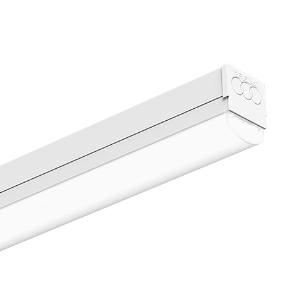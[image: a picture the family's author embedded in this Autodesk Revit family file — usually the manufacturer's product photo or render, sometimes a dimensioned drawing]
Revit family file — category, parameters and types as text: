
# Revit family: 3f_filippi_-_3f_zeta_d_3f_filippi_-_10875_-_3f_zeta_d_2x9_led_l605
name_source: partatom
category: Lighting Fixtures
units: mm (PartAtom-declared; Revit-internal decimal feet)

## family parameters
Cut with Voids When Loaded = No
Host = Face
Light Source = No
Part Type = Normal
Room Calculation Point = No
Round Connector Dimension = Use Diameter
Shared = No

## types (1)
- 3F Filippi - 3F Zeta D (1 x LED, 2418 lm, 20 W, 4000 K)
    Apparent Load = 20 VA
    Approval mark = CE
    CIE Flux Codes = 42 71 90 91 100
    Color Rendering = 80
    Color Temperature = 4000 K
    Control Gear = Electronic ballast
    Default Elevation = 1800 mm
    Description = ILLUMINOTECHNICAL
Luminous efficiency 100% (DLOR 91%, ULOR 9%).
Initial luminous flux of the luminaire 2418 lm.
Diffused symmetric distribution.
Installation Interdistance Transv.D = 1.31 x hu - Long.D = 1.25 x hu.
Tabular UGR (CIE 117 - 4H-8H; S=0.25H; 70/50/20): RUG 26.1 - 24.2.
Beam angle: 130° - 112°.
Luminous efficacy 121 lm/W.
Lifetime (L93/B10): 30000 h. (tq+25°C)
Lifetime (L90/B10): 50000 h. (tq+25°C)
Lifetime (L85/B10): 80000 h. (tq+25°C)
Lifetime (L80/B10): 100000 h. (tq+25°C)
Sudden decreased luminous flux after 50000 hours: 0% (C0).
Photobiological safety in compliance with IEC/TR 62778: RG0 risk exempt, (IEC 62471).
In compliance with IEC/EN 62722-2-1 - IEC/EN 62717 standards.

SOURCE
2 linear LED modules 9W/840.
Energy efficiency class (UE 2019/2020 - UE 2019/2015): D.
CIE 13.3 Colour rendering index: CRI >80 (R9 <50%).
IES TM-30 Fidelity Index: Rf = 84 Rg = 95.
CCT nominal colour temperature 4000 K.
Colour initial tolerance (MacAdam): SDCM 3.

MECHANICAL
Housing in hot-galvanised steel, painted in white polyester, obtained through rolling process.
Light unit in hot-galvanised steel, painted in white polyester base with fixing springs and retractable safety hooks in stainless steel.
Curved screen in self-extinguishing polycarbonate, UV stabilised, opal, with smooth outer surface.
End caps in white polycarbonate.
Pair of stainless steel sliding brackets with sliding block screws.
Luminaire with limited surface temperature. - D - (EN 60598-2-24)
Dimensions: 605x62 mm, height 81 mm. Weight 1.535 kg.
IP40 protection degree.
Mechanical strength to impacts IK06 (1 joule).
Glow-wire test resistance 850°C.

ELECTRICAL
Halogen Free electronic wiring 230V-50/60Hz, power factor 0.90, THD <25%, constant output current, SELV, class I, 1 driver.
Power of the luminaire 20 W.
ENEC - CE.
SAFE FLICKER: PstLM=<1 and SVM=<0.4 (IEC TR 61547-1 and IEC TR 63158), to ensure a more comfortable and safe light.
Luminaire compliant with EN 60598-2-22 for power supply from a centralised emergency system CPSS (Central Power Supply System), not incorporated in the luminaire - high risk areas excluded. The default power and flux are 100% in AC and 100% in DC.
Ambient temperature from 0°C to +25°C.
Temperature class T6 max 85°C.
Relative humidity UR: <85%.

INSTALLATION
Ceiling / Suspended / Wall.
All accessories dedicated to this product are available on the Catalog and on our website www.3F-Filippi.com.

APPLICATIONS
Suitable product for food production plants (HACCP), IFS (Food Version 6), BRC (GSFS Food Version 7).
In commercial environments, exhibition areas, shops and stores.

WARNING
Luminaire designed for disposal/recycling at end-of-life.
Replaceable (LED only) light source by a professional. Replaceable control gear by a professional.
    Height = 81 mm
    Lamp = 1 x LED
    Lamp Light Flux = 2418 lm
    Lamp Power = 20 W
    Lamp count = 1
    Length = 605 mm
    Lifetime = 50000 h
    Luminous efficacy = 121 lm/W
    Manufacturer = 3F Filippi
    ModVariant = No
    Model = 3F Filippi - 10875 - 3F Zeta D 2x9 LED L605
    Mounting Place = Ceiling
    Mounting Type = Pendant
    Number of Poles = 1
    OnlyDefault = Yes
    Power Factor = 1
    Product Name = 3F Filippi - 3F Zeta D
    Product group = pendant luminaire
    ProductGroupID = 9
    Protection Class = Protection class I
    Protection Degree = IP 40
    RLX_Detail_Level = 1
    RLX_Emergency_Light_Flux = 0 lm
    RLX_Emergency_Type = 0
    RLX_Emergency_Type_DB = No
    RlxData = <blob elided: 33413 chars, md5=e7046a50>
    Socket = socket
    Standby Power = 0 W
    System Light Flux = 2418 lm
    System Power = 20 W
    Type Comments = Product without accessories
    Type Image = 3ffilippi_3f_zeta_d.jpg
    URL = http://relux.com
    VarID = ---
    Voltage = 0 V
    Weight = 0.00 kg
    Width = 62 mm  [stored 0.203412 ft]

note: [stored X ft] marks values corroborated as IEEE doubles in the binary element streams (Revit-internal decimal feet)

## geometry (parser evidence)
native form markers: Blend x4, Sweep x10
no freeform markers — native parametric forms only
